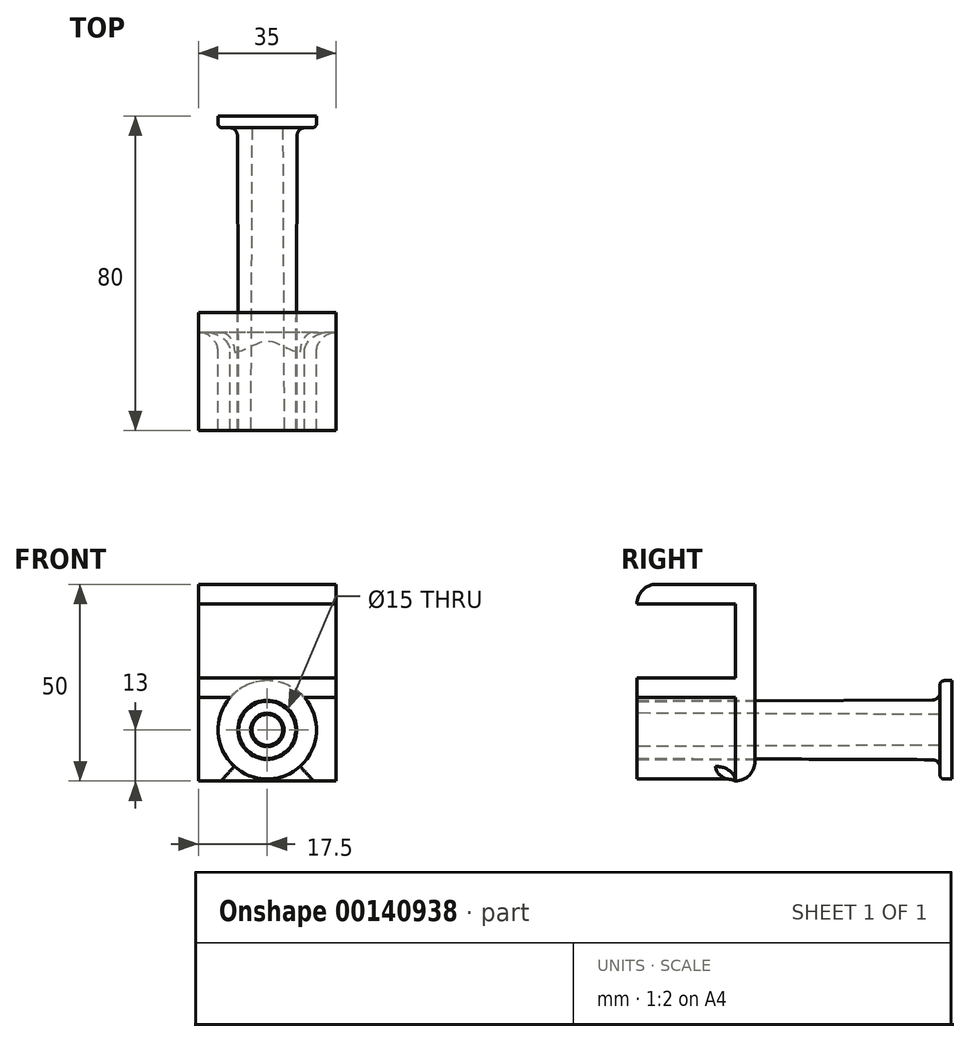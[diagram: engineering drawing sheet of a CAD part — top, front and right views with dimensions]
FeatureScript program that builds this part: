
annotation { "Feature Type Name" : "Feature", "Feature Type Description" : "" }
export const myFeature = defineFeature(function(context is Context, id is Id, definition is map)
    precondition{}
    {
        {
            var Q0;
            Q0=qCreatedBy(makeId("Right.planeOp"),FACE);
            var sketch = newSketch(context, id + "F0", { "sketchPlane" : qUnion([Q0])});
            skLineSegment(sketch, "E0.bottom", {"start": v(0, 0) * mm, "end": v(-5, 0) * mm});
            skLineSegment(sketch, "E0.top", {"start": v(0, 50) * mm, "end": v(-5, 50) * mm});
            skLineSegment(sketch, "E0.left", {"start": v(0, 0) * mm, "end": v(0, 50) * mm});
            skLineSegment(sketch, "E0.right", {"start": v(-5, 0) * mm, "end": v(-5, 50) * mm});
            skLineSegment(sketch, "E1.bottom", {"start": v(-5, 50) * mm, "end": v(-30, 50) * mm});
            skLineSegment(sketch, "E1.top", {"start": v(-5, 45) * mm, "end": v(-30, 45) * mm});
            skLineSegment(sketch, "E1.left", {"start": v(-5, 50) * mm, "end": v(-5, 45) * mm});
            skLineSegment(sketch, "E1.right", {"start": v(-30, 50) * mm, "end": v(-30, 45) * mm});
            skLineSegment(sketch, "E2.bottom", {"start": v(-5, 26.2) * mm, "end": v(-30, 26.2) * mm});
            skLineSegment(sketch, "E2.top", {"start": v(-5, 21.2) * mm, "end": v(-30, 21.2) * mm});
            skLineSegment(sketch, "E2.left", {"start": v(-5, 26.2) * mm, "end": v(-5, 21.2) * mm});
            skLineSegment(sketch, "E2.right", {"start": v(-30, 26.2) * mm, "end": v(-30, 21.2) * mm});
            skSolve(sketch);
        }
        {
            var Q0;
            Q0 = qSketchRegion(id + "F0", true);
            extrude(context, id + "F1", {"entities" : qUnion([Q0]), "depth" : 35 * mm});
        }
        {
            var Q0;
            Q0=makeQuery(id+"F1.opExtrude","SWEPT_FACE",FACE,{"disambiguationData":[OSD([sQuery(id+"F0.wireOp",EDGE,"E0.left")])]});
            var sketch = newSketch(context, id + "F2", { "sketchPlane" : qUnion([Q0])});
            skCircle(sketch, "E3", {"center": v(-17.5, 13) * mm, "radius": 7.5 * mm});
            skCircle(sketch, "E4", {"center": v(-17.5, 13) * mm, "radius": 12.5 * mm});
            skSolve(sketch);
        }
        {
            var Q0;
            Q0 = qSketchRegion(id + "F2", true);
            var Q1;
            Q1=makeQuery(id+"F1.opExtrude","SWEPT_FACE",FACE,{"disambiguationData":[OSD([sQuery(id+"F0.wireOp",EDGE,"E2.right")])]});
            extrude(context, id + "F3", {"entities" : qUnion([Q0]), "operationType" : NewBodyOperationType.ADD, "endBound" : BoundingType.UP_TO_SURFACE, "oppositeDirection" : true, "endBoundEntityFace" : qUnion([Q1]), "depth" : 30 * mm});
        }
        {
            var Q0;
            {var subQ0=sQuery(id+"F0.wireOp",EDGE,"E2.right");Q0=makeQuery(id+"F3.boolean.opBoolean","MERGE",FACE,{"derivedFrom":[makeQuery(id+"F1.opExtrude","SWEPT_FACE",FACE,{"disambiguationData":[OSD([subQ0])]}),makeQuery(id+"F3.opExtrude","CAP_FACE",FACE,{"disambiguationData":[OSD([subQ0])],"isStart":false})]});}
            var sketch = newSketch(context, id + "F4", { "sketchPlane" : qUnion([Q0])});
            skCircle(sketch, "E5", {"center": v(17.5, 13) * mm, "radius": 7.5 * mm});
            skSolve(sketch);
        }
        {
            var Q0;
            Q0 = qSketchRegion(id + "F4", true);
            var Q1;
            Q1=makeQuery(id+"F1.opExtrude","SWEPT_FACE",FACE,{"disambiguationData":[OSD([sQuery(id+"F0.wireOp",EDGE,"E0.left")])]});
            extrude(context, id + "F5", {"entities" : qUnion([Q0]), "operationType" : NewBodyOperationType.REMOVE, "endBound" : BoundingType.UP_TO_SURFACE, "oppositeDirection" : true, "endBoundEntityFace" : qUnion([Q1]), "depth" : 25 * mm});
        }
        {
            var Q0;
            Q0=makeQuery(id+"F1.opExtrude","SWEPT_EDGE",EDGE,{"disambiguationData":[OSD([sQuery(id+"F0.wireOp",EDGE,"E1.bottom"),sQuery(id+"F0.wireOp",EDGE,"E1.right")])]});
            var Q1;
            Q1=makeQuery(id+"F1.opExtrude","SWEPT_EDGE",EDGE,{"disambiguationData":[OSD([sQuery(id+"F0.wireOp",EDGE,"E0.bottom"),sQuery(id+"F0.wireOp",EDGE,"E0.left")])]});
            fillet(context, id + "F6", {"entities" : qUnion([Q0, Q1]), "radius" : 5 * mm, "tangentPropagation" : true, "allowEdgeOverflow" : false});
        }
        {
            var Q0;
            {var subQ0=sQuery(id+"F0.wireOp",EDGE,"E0.right");Q0=makeQuery(id+"F3.boolean.opBoolean","INTERSECT",EDGE,{"derivedFrom":[makeQuery(id+"F1.opExtrude","SWEPT_FACE",FACE,{"disambiguationData":[OSD([subQ0]),TDD([makeQuery(id+"F0.imprint","IMPRINT",EDGE,{"disambiguationData":[TD([[makeQuery(id+"F0.imprint","INTERSECT",VERTEX,{"derivedFrom":[sQuery(id+"F0.wireOp",EDGE,"E0.bottom"),subQ0]}),-1.0]])],"derivedFrom":subQ0})])]}),makeQuery(id+"F3.opExtrude","SWEPT_FACE",FACE,{"disambiguationData":[OSD([sQuery(id+"F2.wireOp",EDGE,"E4")])]})]});}
            fillet(context, id + "F7", {"entities" : qUnion([Q0]), "radius" : 5 * mm, "tangentPropagation" : true, "allowEdgeOverflow" : false});
        }
        {
            var Q0;
            {var subQ0=sQuery(id+"F0.wireOp",EDGE,"E2.right");Q0=makeQuery(id+"F3.boolean.opBoolean","MERGE",FACE,{"derivedFrom":[makeQuery(id+"F1.opExtrude","SWEPT_FACE",FACE,{"disambiguationData":[OSD([subQ0])]}),makeQuery(id+"F3.opExtrude","CAP_FACE",FACE,{"disambiguationData":[OSD([subQ0])],"isStart":false})]});}
            var sketch = newSketch(context, id + "F8", { "sketchPlane" : qUnion([Q0])});
            skCircle(sketch, "E6", {"center": v(17.5, 13) * mm, "radius": 7.25 * mm});
            skCircle(sketch, "E7", {"center": v(17.5, 13) * mm, "radius": 4.25 * mm});
            skSolve(sketch);
        }
        {
            var Q0;
            Q0 = qSketchRegion(id + "F8", true);
            extrude(context, id + "F9", {"entities" : qUnion([Q0]), "oppositeDirection" : true, "depth" : 80 * mm, "hasDraft" : true, "draftAngle" : .25 * degree});
        }
        {
            var Q0;
            Q0=makeQuery(id+"F9.opExtrude","CAP_FACE",FACE,{"disambiguationData":[OSD([sQuery(id+"F8.wireOp",EDGE,"E6"),sQuery(id+"F8.wireOp",EDGE,"E7")])],"isStart":false});
            var sketch = newSketch(context, id + "F10", { "sketchPlane" : qUnion([Q0])});
            skCircle(sketch, "E8", {"center": v(-17.5, 13) * mm, "radius": 12.5 * mm});
            skSolve(sketch);
        }
        {
            var Q0;
            Q0 = qSketchRegion(id + "F10", true);
            extrude(context, id + "F11", {"entities" : qUnion([Q0]), "operationType" : NewBodyOperationType.ADD, "oppositeDirection" : true, "depth" : 3 * mm});
        }
        {
            var Q0;
            Q0=makeQuery(id+"F11.boolean.opBoolean","INTERSECT",EDGE,{"derivedFrom":[makeQuery(id+"F9.opExtrude","SWEPT_FACE",FACE,{"disambiguationData":[OSD([sQuery(id+"F8.wireOp",EDGE,"E6")])]}),makeQuery(id+"F11.opExtrude","CAP_FACE",FACE,{"disambiguationData":[OSD([sQuery(id+"F10.wireOp",EDGE,"E8")])],"isStart":false})]});
            fillet(context, id + "F12", {"entities" : qUnion([Q0]), "radius" : 2 * mm, "tangentPropagation" : true, "allowEdgeOverflow" : false});
        }
        {
            var Q0;
            Q0=makeQuery(id+"F11.opExtrude","CAP_EDGE",EDGE,{"disambiguationData":[OSD([sQuery(id+"F10.wireOp",EDGE,"E8")])],"isStart":false});
            fillet(context, id + "F13", {"entities" : qUnion([Q0]), "radius" : 1 * mm, "tangentPropagation" : true, "allowEdgeOverflow" : false});
        }
    });
